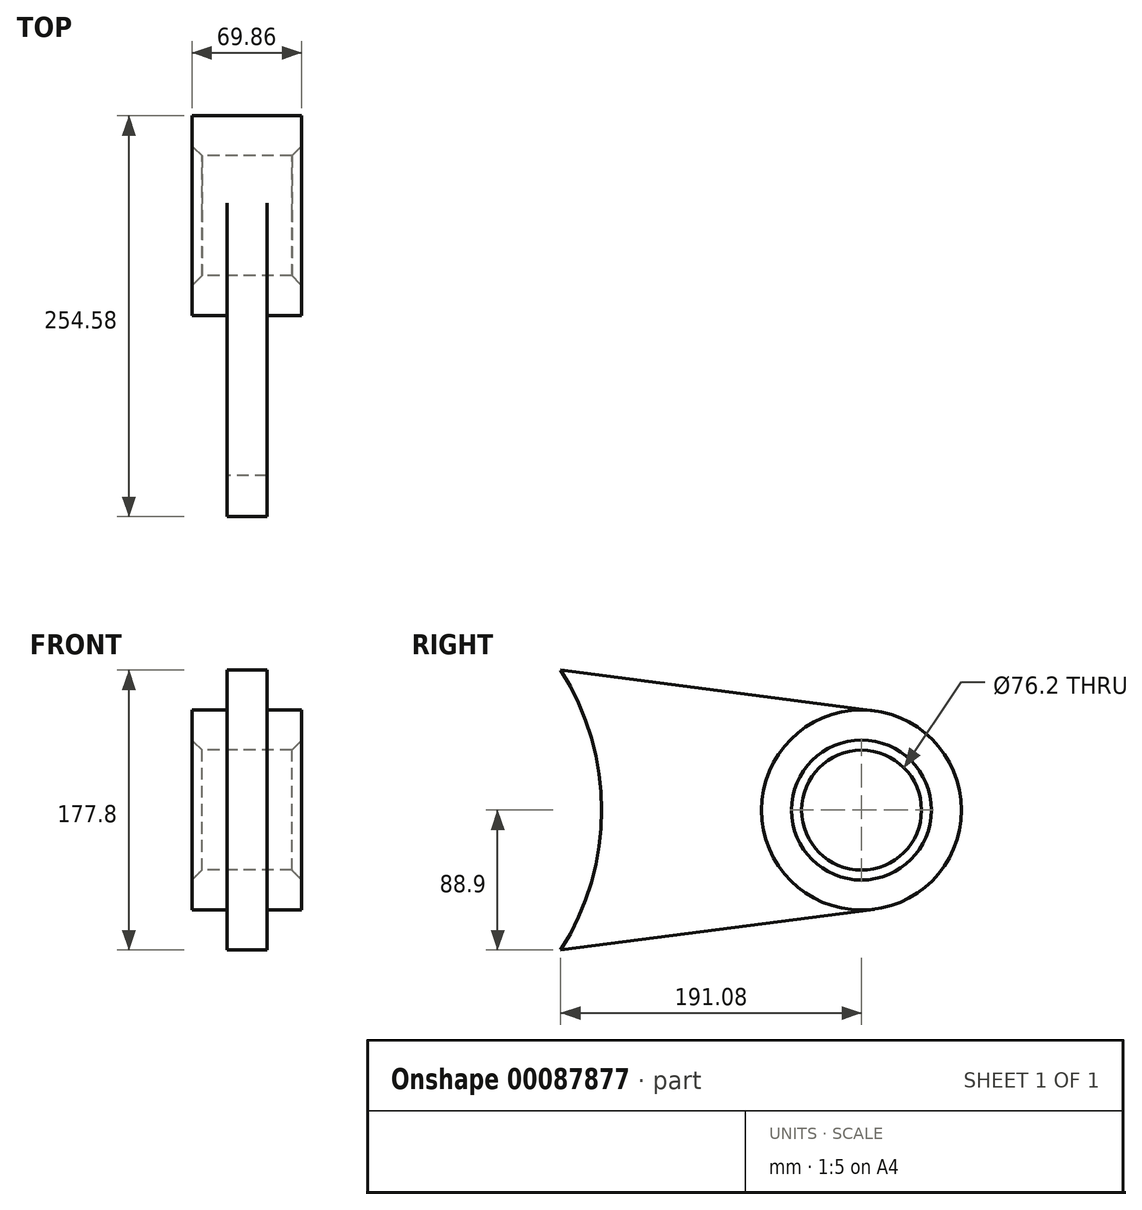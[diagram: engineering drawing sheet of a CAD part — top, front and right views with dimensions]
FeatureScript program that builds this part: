
annotation { "Feature Type Name" : "Feature", "Feature Type Description" : "" }
export const myFeature = defineFeature(function(context is Context, id is Id, definition is map)
    precondition{}
    {
        {
            var Q0;
            Q0=qCreatedBy(makeId("Right.planeOp"),FACE);
            var sketch = newSketch(context, id + "F0", { "sketchPlane" : qUnion([Q0])});
            skArc(sketch, "E0", {"start": v(139.12, -88.9) * mm, "mid": v(165.1, 0) * mm, "end": v(139.12, 88.9) * mm});
            skLineSegment(sketch, "E1", {"start": v(0, 0) * mm, "end": v(330.2, 0) * mm, "construction": true});
            skArc(sketch, "E2", {"start": v(338.4, -62.97) * mm, "mid": v(393.7, 0) * mm, "end": v(338.4, 62.97) * mm});
            skLineSegment(sketch, "E3.0", {"start": v(0, 88.9) * mm, "end": v(330.2, 88.9) * mm, "construction": true});
            skLineSegment(sketch, "E4.MirrorCS", {"start": v(0, -88.9) * mm, "end": v(330.2, -88.9) * mm, "construction": true});
            skLineSegment(sketch, "E5", {"start": v(139.12, 88.9) * mm, "end": v(350.34, 61.41) * mm});
            skLineSegment(sketch, "E6.MirrorCS", {"start": v(139.12, -88.9) * mm, "end": v(350.34, -61.41) * mm});
            skCircle(sketch, "E7", {"center": v(330.2, 0) * mm, "radius": 38.1 * mm});
            skSolve(sketch);
        }
        {
            var Q0;
            {var subQ1=sQuery(id+"F0.wireOp",EDGE,"E0");Q0=makeQuery(id+"F0.imprint","IMPRINT",FACE,{"disambiguationData":[TD([[makeQuery(id+"F0.imprint","IMPRINT",EDGE,{"derivedFrom":subQ1}),-1.0]])]});}
            extrude(context, id + "F1", {"entities" : qUnion([Q0]), "endBound" : BoundingType.SYMMETRIC, "depth" : 25.4 * mm});
        }
        {
            var Q0;
            Q0=qCreatedBy(makeId("Right.planeOp"),FACE);
            var sketch = newSketch(context, id + "F2", { "sketchPlane" : qUnion([Q0])});
            skCircle(sketch, "E8.0", {"center": v(330.2, 0) * mm, "radius": 38.1 * mm});
            skCircle(sketch, "E9", {"center": v(330.2, 0) * mm, "radius": 63.5 * mm});
            skSolve(sketch);
        }
        {
            var Q0;
            Q0 = qSketchRegion(id + "F2", true);
            extrude(context, id + "F3", {"entities" : qUnion([Q0]), "operationType" : NewBodyOperationType.ADD, "endBound" : BoundingType.SYMMETRIC, "depth" : 69.85 * mm});
        }
        {
            var Q0;
            Q0=makeQuery(id+"F3.opExtrude","CAP_EDGE",EDGE,{"disambiguationData":[OSD([sQuery(id+"F2.wireOp",EDGE,"E8.0")])],"isStart":true});
            var Q1;
            Q1=makeQuery(id+"F3.opExtrude","CAP_EDGE",EDGE,{"disambiguationData":[OSD([sQuery(id+"F2.wireOp",EDGE,"E8.0")])],"isStart":false});
            chamfer(context, id + "F4", {"entities" : qUnion([Q0, Q1]), "width" : 6.35 * mm, "tangentPropagation" : true});
        }
    });
